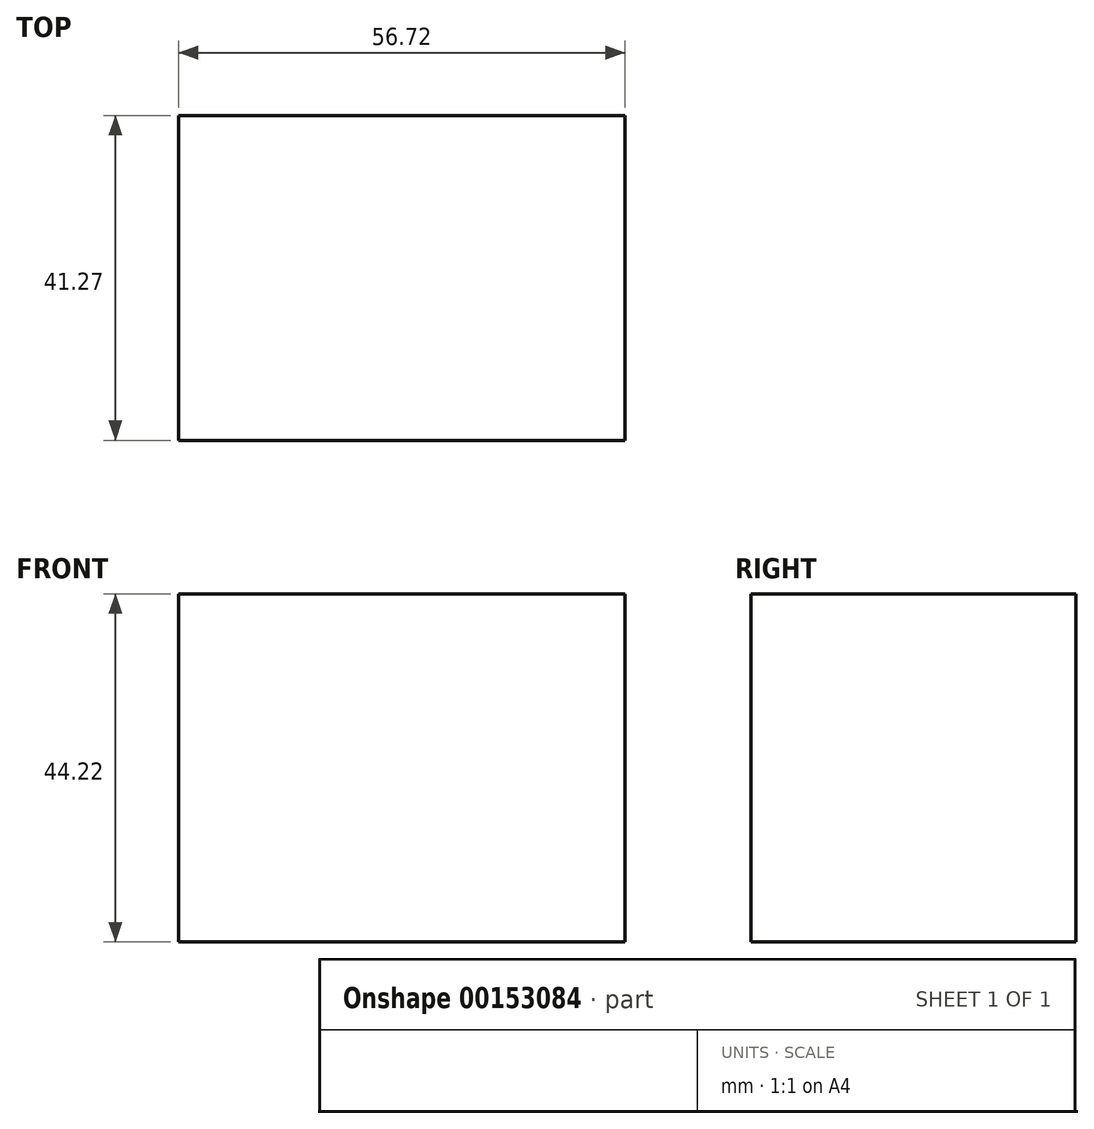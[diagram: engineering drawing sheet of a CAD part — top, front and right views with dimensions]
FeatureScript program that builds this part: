
annotation { "Feature Type Name" : "Feature", "Feature Type Description" : "" }
export const myFeature = defineFeature(function(context is Context, id is Id, definition is map)
    precondition{}
    {
        {
            var Q0;
            Q0=qCreatedBy(makeId("Front.planeOp"),FACE);
            var sketch = newSketch(context, id + "F0", { "sketchPlane" : qUnion([Q0])});
            skLineSegment(sketch, "E0.bottom", {"start": v(0, 0) * mm, "end": v(56.72, 0) * mm});
            skLineSegment(sketch, "E0.top", {"start": v(0, 44.22) * mm, "end": v(56.72, 44.22) * mm});
            skLineSegment(sketch, "E0.left", {"start": v(0, 0) * mm, "end": v(0, 44.22) * mm});
            skLineSegment(sketch, "E0.right", {"start": v(56.72, 0) * mm, "end": v(56.72, 44.22) * mm});
            skSolve(sketch);
        }
        {
            var Q0;
            Q0 = qSketchRegion(id + "F0", true);
            extrude(context, id + "F1", {"entities" : qUnion([Q0]), "oppositeDirection" : true, "depth" : 41.27 * mm});
        }
    });
